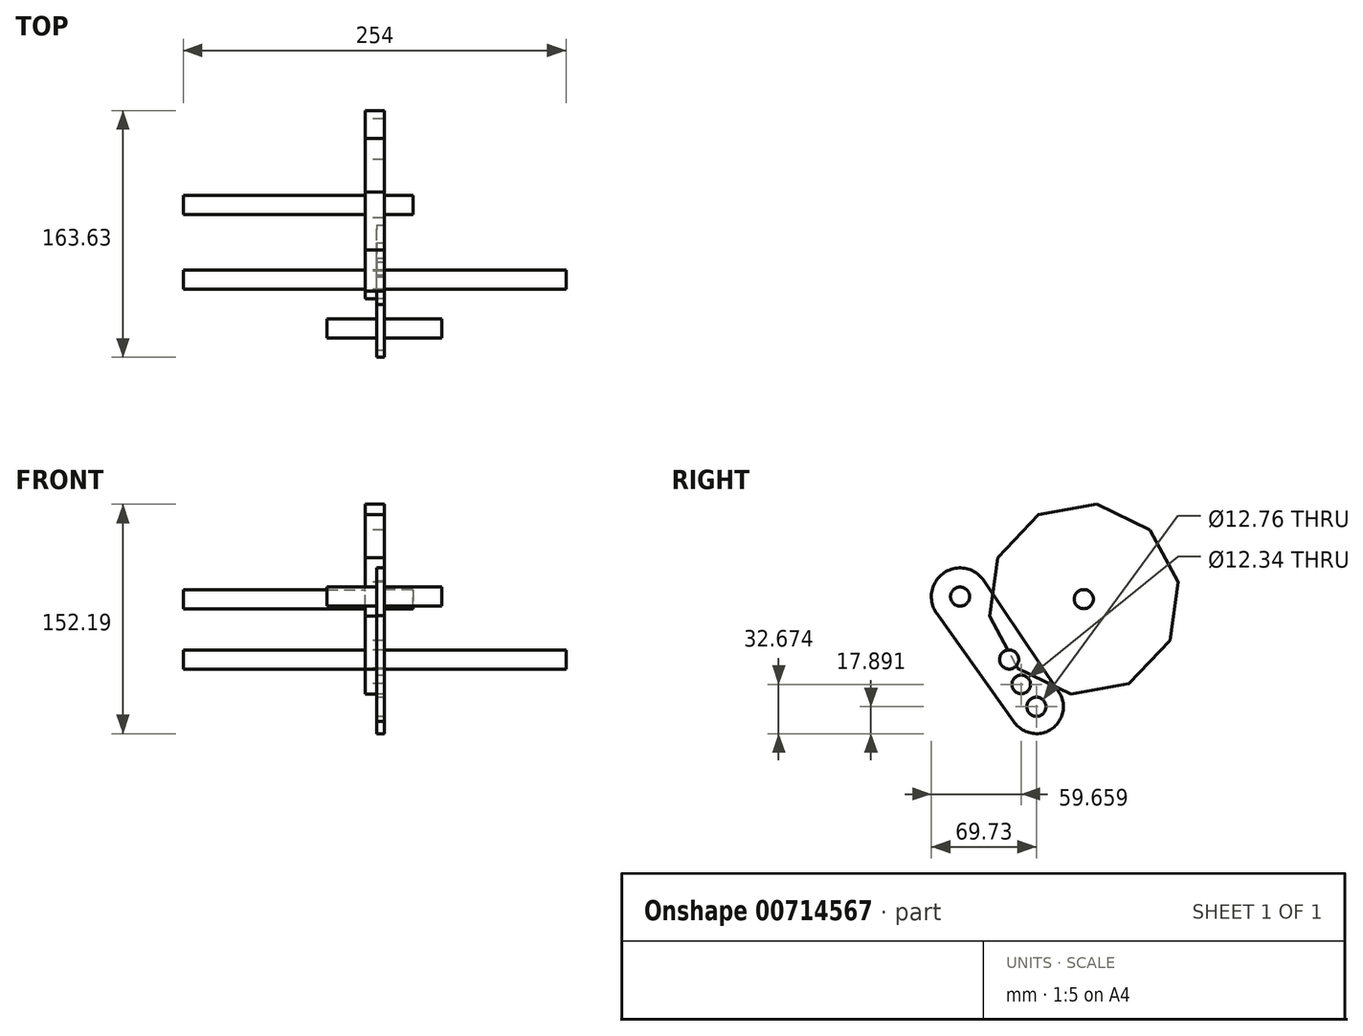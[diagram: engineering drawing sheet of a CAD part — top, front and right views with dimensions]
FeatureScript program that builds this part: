
annotation { "Feature Type Name" : "Feature", "Feature Type Description" : "" }
export const myFeature = defineFeature(function(context is Context, id is Id, definition is map)
    precondition{}
    {
        {
            var Q0;
            Q0=qCreatedBy(makeId("Right.planeOp"),FACE);
            var sketch = newSketch(context, id + "F0", { "sketchPlane" : qUnion([Q0])});
            skCircle(sketch, "E0", {"center": v(0, 0) * mm, "radius": 6.35 * mm});
            skSolve(sketch);
        }
        {
            var Q0;
            Q0=makeQuery(id+"F0.imprint","IMPRINT",FACE,{"disambiguationData":[TD([[makeQuery(id+"F0.imprint","IMPRINT",EDGE,{"derivedFrom":sQuery(id+"F0.wireOp",EDGE,"E0")}),1.0]])]});
            extrude(context, id + "F1", {"entities" : qUnion([Q0]), "endBound" : BoundingType.SYMMETRIC, "depth" : 254 * mm, "offsetDistance" : 25.4 * mm});
        }
        {
            var Q0;
            Q0=qCreatedBy(makeId("Right.planeOp"),FACE);
            var sketch = newSketch(context, id + "F2", { "sketchPlane" : qUnion([Q0])});
            skCircle(sketch, "E1.cCircle", {"center": v(49.48, 40.05) * mm, "radius": 63.5 * mm, "construction": true});
            skLineSegment(sketch, "E1.0", {"start": v(5.58, -5.83) * mm, "end": v(-13, 28.74) * mm});
            skLineSegment(sketch, "E1.1", {"start": v(-13, 28.74) * mm, "end": v(-7.72, 67.62) * mm});
            skLineSegment(sketch, "E1.2", {"start": v(-7.72, 67.62) * mm, "end": v(19.41, 95.98) * mm});
            skLineSegment(sketch, "E1.3", {"start": v(19.41, 95.98) * mm, "end": v(58.03, 102.97) * mm});
            skLineSegment(sketch, "E1.4", {"start": v(58.03, 102.97) * mm, "end": v(93.38, 85.93) * mm});
            skLineSegment(sketch, "E1.5", {"start": v(93.38, 85.93) * mm, "end": v(111.96, 51.37) * mm});
            skLineSegment(sketch, "E1.6", {"start": v(111.96, 51.37) * mm, "end": v(106.68, 12.48) * mm});
            skLineSegment(sketch, "E1.7", {"start": v(106.68, 12.48) * mm, "end": v(79.55, -15.88) * mm});
            skLineSegment(sketch, "E1.8", {"start": v(79.55, -15.88) * mm, "end": v(40.93, -22.87) * mm});
            skLineSegment(sketch, "E1.9", {"start": v(40.93, -22.87) * mm, "end": v(5.58, -5.83) * mm});
            skCircle(sketch, "E2", {"center": v(49.48, 40.05) * mm, "radius": 6.35 * mm});
            skSolve(sketch);
        }
        {
            var Q0;
            Q0=makeQuery(id+"F2.imprint","IMPRINT",FACE,{"disambiguationData":[TD([[makeQuery(id+"F2.imprint","IMPRINT",EDGE,{"derivedFrom":sQuery(id+"F2.wireOp",EDGE,"E1.0")}),-1.0]])]});
            var sketch = newSketch(context, id + "F3", { "sketchPlane" : qUnion([Q0])});
            skSolve(sketch);
        }
        {
            var Q0;
            Q0=makeQuery(id+"F3.imprint","IMPRINT",FACE,{"disambiguationData":[TD([[makeQuery(id+"F3.imprint","IMPRINT",EDGE,{"derivedFrom":makeQuery(id+"F2.imprint","IMPRINT",EDGE,{"derivedFrom":sQuery(id+"F2.wireOp",EDGE,"E1.0")})}),-1.0]])]});
            extrude(context, id + "F4", {"entities" : qUnion([Q0]), "endBound" : BoundingType.SYMMETRIC, "depth" : 12.7 * mm, "offsetDistance" : 25.4 * mm});
        }
        {
            var Q0;
            Q0=makeQuery(id+"F3.imprint","IMPRINT",FACE,{"disambiguationData":[TD([[makeQuery(id+"F3.imprint","IMPRINT",EDGE,{"derivedFrom":makeQuery(id+"F2.imprint","IMPRINT",EDGE,{"derivedFrom":sQuery(id+"F2.wireOp",EDGE,"E2")})}),1.0]])]});
            extrude(context, id + "F5", {"entities" : qUnion([Q0]), "operationType" : NewBodyOperationType.ADD, "depth" : 25.4 * mm, "offsetDistance" : 25.4 * mm});
        }
        {
            var Q0;
            Q0=makeQuery(id+"F3.imprint","IMPRINT",FACE,{"disambiguationData":[TD([[makeQuery(id+"F3.imprint","IMPRINT",EDGE,{"derivedFrom":makeQuery(id+"F2.imprint","IMPRINT",EDGE,{"derivedFrom":sQuery(id+"F2.wireOp",EDGE,"E2")})}),1.0]])]});
            extrude(context, id + "F6", {"entities" : qUnion([Q0]), "operationType" : NewBodyOperationType.ADD, "oppositeDirection" : true, "depth" : 127 * mm, "offsetDistance" : 25.4 * mm});
        }
        {
            var Q0;
            Q0=makeQuery(id+"F4.opExtrude","CAP_FACE",FACE,{"disambiguationData":[OSD([sQuery(id+"F2.wireOp",EDGE,"E1.0"),sQuery(id+"F2.wireOp",EDGE,"E1.1"),sQuery(id+"F2.wireOp",EDGE,"E1.2"),sQuery(id+"F2.wireOp",EDGE,"E1.3"),sQuery(id+"F2.wireOp",EDGE,"E1.4"),sQuery(id+"F2.wireOp",EDGE,"E1.5"),sQuery(id+"F2.wireOp",EDGE,"E1.6"),sQuery(id+"F2.wireOp",EDGE,"E1.7"),sQuery(id+"F2.wireOp",EDGE,"E1.8"),sQuery(id+"F2.wireOp",EDGE,"E1.9"),sQuery(id+"F2.wireOp",EDGE,"E2")])],"isStart":false});
            var sketch = newSketch(context, id + "F7", { "sketchPlane" : qUnion([Q0])});
            skCircle(sketch, "E3", {"center": v(18.06, -31.33) * mm, "radius": 6.38 * mm});
            skCircle(sketch, "E4", {"center": v(18.06, -31.33) * mm, "radius": 17.89 * mm});
            skCircle(sketch, "E5", {"center": v(-32.62, 41.71) * mm, "radius": 19.05 * mm});
            skLineSegment(sketch, "E6", {"start": v(-49.24, 32.4) * mm, "end": v(4.03, -42.42) * mm});
            skLineSegment(sketch, "E7", {"start": v(-16.96, 52.56) * mm, "end": v(32.89, -21.32) * mm});
            skCircle(sketch, "E8", {"center": v(7.99, -16.55) * mm, "radius": 6.17 * mm});
            skCircle(sketch, "E9", {"center": v(-32.62, 41.71) * mm, "radius": 6.35 * mm});
            skSolve(sketch);
        }
        {
            var Q0;
            Q0 = qSketchRegion(id + "F7", true);
            extrude(context, id + "F8", {"entities" : qUnion([Q0]), "oppositeDirection" : true, "depth" : 5.08 * mm, "offsetDistance" : 25.4 * mm});
        }
        {
            var Q0;
            Q0=makeQuery(id+"F7.imprint","IMPRINT",FACE,{"disambiguationData":[TD([[makeQuery(id+"F7.imprint","IMPRINT",EDGE,{"derivedFrom":sQuery(id+"F7.wireOp",EDGE,"E9")}),1.0]])]});
            extrude(context, id + "F9", {"entities" : qUnion([Q0]), "operationType" : NewBodyOperationType.ADD, "endBound" : BoundingType.SYMMETRIC, "depth" : 76.2 * mm, "offsetDistance" : 25.4 * mm});
        }
    });
